# Revit family: RBA4901-Straight-Series
name_source: partatom
category: Plumbing Fixtures
units: mm (PartAtom-declared; Revit-internal decimal feet)

## family parameters
Always vertical = Yes
Cut with Voids When Loaded = No
Part Type = Normal
Room Calculation Point = No
Round Connector Dimension = Use Diameter
Shared = No
Work Plane-Based = No

## types (9) — shared parameters
Diameter = 32 mm  [stored 0.104987 ft]
Manufacturer = RBA Group
Materials & Finishes = Stainless Steel Satin Finish
zero-valued in all types: Default Elevation

## per-type parameters (varying)
| type | Description | Lgth | Model | Modified Issue | URL |
| RBA4901-040 | Straight Grab Rail 400mm | 400 mm  [stored 1.31234 ft] | RBA4000-040 | 20191108.1 | www.rba.com.au |
| RBA4901-120 | Straight Grab Rail 1200mm | 1200 mm | RBA4000-120 | 20191004.01 | http://www.rba.com.au |
| RBA4901-100 | Straight Grab Rail 1000mm | 1000 mm  [stored 3.28084 ft] | RBA4000-100 | 20191004.01 | http://www.rba.com.au |
| RBA4901-080 | Straight Grab Rail 800mm | 800 mm  [stored 2.62467 ft] | RBA4000-080 | 20191004.01 | http://www.rba.com.au |
| RBA4901-090 | Straight Grab Rail 900mm | 900 mm  [stored 2.95276 ft] | RBA4000-090 | 20191004.01 | www.rba.com.au |
| RBA4901-070 | Straight Grab Rail 750mm | 700 mm  [stored 2.29659 ft] | RBA4000-075 | 20191004.01 | www.rba.com.au |
| RBA4901-060 | Steri+ShieldTM Straight Grab Rail, Satin | 600 mm  [stored 1.9685 ft] | RBA4901-Straight-Series |  | www.rba.com.au |
| RBA4901-045 | Straight Grab Rail 450mm | 200 mm  [stored 0.656168 ft] | RBA4000-045 | 20191004.01 | www.rba.com.au |
| RBA4901-030 | Straight Grab Rail 300mm | 300 mm | RBA4000-030 | 20190510.1 | www.rba.com.au |

note: [stored X ft] marks values corroborated as IEEE doubles in the binary element streams (Revit-internal decimal feet)

## geometry (parser evidence)
native form markers: Blend x2, Sweep x3
no freeform markers — native parametric forms only
